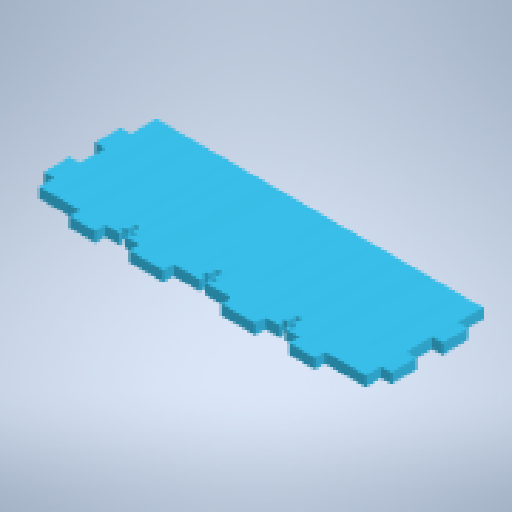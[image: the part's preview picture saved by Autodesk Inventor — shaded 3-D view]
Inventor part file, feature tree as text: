
AUTODESK INVENTOR PART (.ipt)
format: ipt  version: 2024.2 (Build 282272000, 272)  size: 351,232 bytes
history: native  units: mm
features: other x1, extrude x1, sketch x1
ambient origin geometry x8: Origin, YZ Plane, XZ Plane, XY Plane, X Axis, Y Axis, Z Axis, Center Point
bodies: Body1 (feature_tree)
feature tree (3):
  other  "Твердое тело1"
  extrude  "Выдавливание1"  Depth=204.0mm
  sketch  "Эскиз1"
